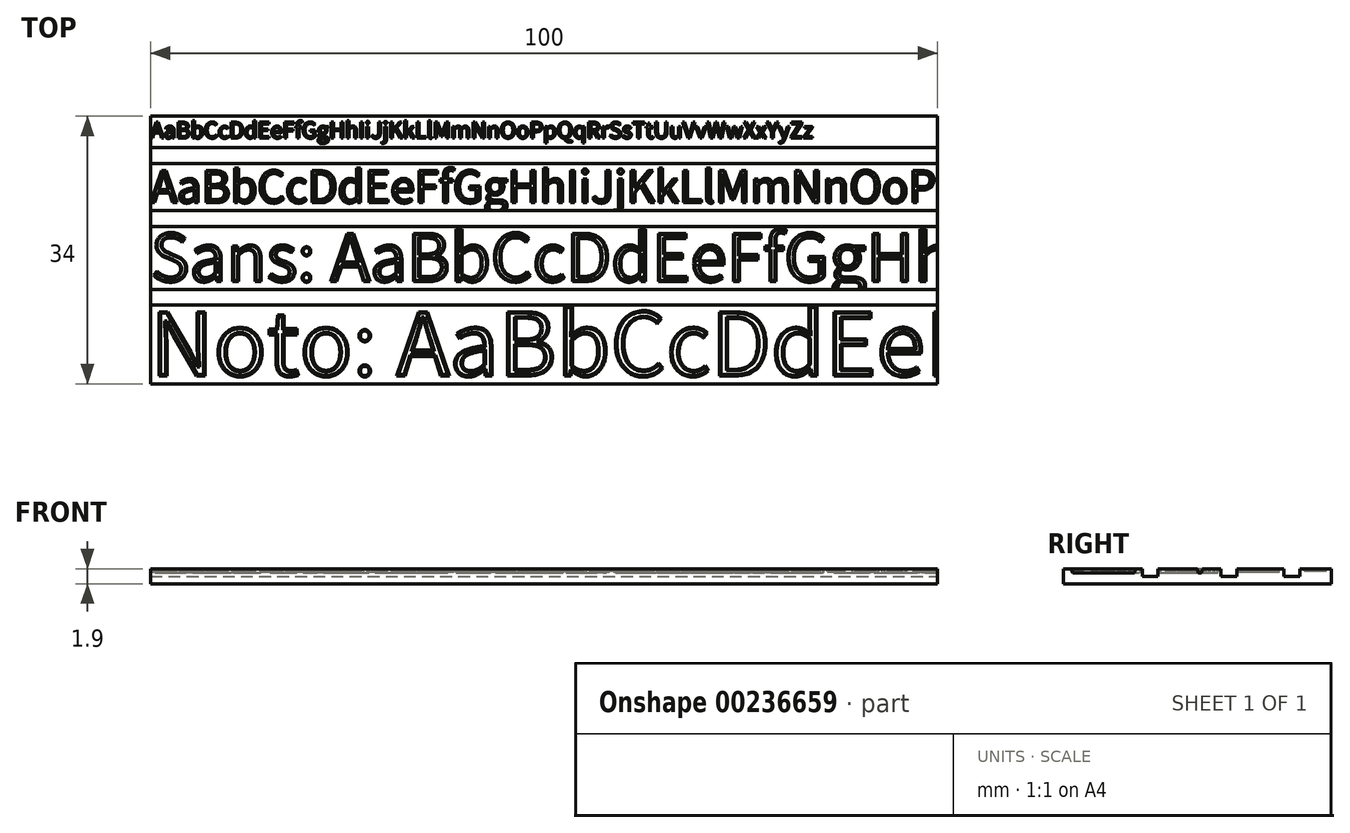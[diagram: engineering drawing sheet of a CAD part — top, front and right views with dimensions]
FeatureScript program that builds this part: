
annotation { "Feature Type Name" : "Feature", "Feature Type Description" : "" }
export const myFeature = defineFeature(function(context is Context, id is Id, definition is map)
    precondition{}
    {
        {
            var Q0;
            Q0=qCreatedBy(makeId("Top.planeOp"),FACE);
            var sketch = newSketch(context, id + "F0", { "sketchPlane" : qUnion([Q0])});
            skLineSegment(sketch, "E0.bottom", {"start": v(0, 0) * mm, "end": v(100, 0) * mm});
            skLineSegment(sketch, "E0.top", {"start": v(0, 34) * mm, "end": v(100, 34) * mm});
            skLineSegment(sketch, "E0.left", {"start": v(0, 0) * mm, "end": v(0, 34) * mm});
            skLineSegment(sketch, "E0.right", {"start": v(100, 0) * mm, "end": v(100, 34) * mm});
            skSolve(sketch);
        }
        {
            var Q0;
            Q0=makeQuery(id+"F0.imprint","IMPRINT",FACE,{"disambiguationData":[TD([[makeQuery(id+"F0.imprint","IMPRINT",EDGE,{"derivedFrom":sQuery(id+"F0.wireOp",EDGE,"E0.bottom")}),1.0]])]});
            extrude(context, id + "F1", {"entities" : qUnion([Q0]), "depth" : 0.9 * mm});
        }
        {
            var Q0;
            Q0=makeQuery(id+"F1.opExtrude","CAP_FACE",FACE,{"disambiguationData":[OSD([sQuery(id+"F0.wireOp",EDGE,"E0.bottom"),sQuery(id+"F0.wireOp",EDGE,"E0.top"),sQuery(id+"F0.wireOp",EDGE,"E0.left"),sQuery(id+"F0.wireOp",EDGE,"E0.right")])],"isStart":false});
            var sketch = newSketch(context, id + "F2", { "sketchPlane" : qUnion([Q0])});
            skLineSegment(sketch, "E1.bottom", {"start": v(0, 0) * mm, "end": v(100, 0) * mm});
            skLineSegment(sketch, "E1.top", {"start": v(0, 10) * mm, "end": v(100, 10) * mm});
            skLineSegment(sketch, "E1.left", {"start": v(0, 0) * mm, "end": v(0, 10) * mm});
            skLineSegment(sketch, "E1.right", {"start": v(100, 0) * mm, "end": v(100, 10) * mm});
            skLineSegment(sketch, "E2.bottom", {"start": v(0, 12) * mm, "end": v(100, 12) * mm});
            skLineSegment(sketch, "E2.top", {"start": v(0, 20) * mm, "end": v(100, 20) * mm});
            skLineSegment(sketch, "E2.left", {"start": v(0, 12) * mm, "end": v(0, 20) * mm});
            skLineSegment(sketch, "E2.right", {"start": v(100, 12) * mm, "end": v(100, 20) * mm});
            skLineSegment(sketch, "E3.bottom", {"start": v(0, 22) * mm, "end": v(100, 22) * mm});
            skLineSegment(sketch, "E3.top", {"start": v(0, 28) * mm, "end": v(100, 28) * mm});
            skLineSegment(sketch, "E3.left", {"start": v(0, 22) * mm, "end": v(0, 28) * mm});
            skLineSegment(sketch, "E3.right", {"start": v(100, 22) * mm, "end": v(100, 28) * mm});
            skLineSegment(sketch, "E4.bottom", {"start": v(0, 30) * mm, "end": v(100, 30) * mm});
            skLineSegment(sketch, "E4.top", {"start": v(0, 34) * mm, "end": v(100, 34) * mm});
            skLineSegment(sketch, "E4.left", {"start": v(0, 30) * mm, "end": v(0, 34) * mm});
            skLineSegment(sketch, "E4.right", {"start": v(100, 30) * mm, "end": v(100, 34) * mm});
            skSolve(sketch);
        }
        {
            var Q0;
            Q0 = qSketchRegion(id + "F2", true);
            extrude(context, id + "F3", {"entities" : qUnion([Q0]), "operationType" : NewBodyOperationType.ADD, "depth" : 1 * mm});
        }
        {
            var Q0;
            Q0=makeQuery(id+"F3.opExtrude","CAP_FACE",FACE,{"disambiguationData":[OSD([sQuery(id+"F2.wireOp",EDGE,"E1.bottom"),sQuery(id+"F2.wireOp",EDGE,"E1.top"),sQuery(id+"F2.wireOp",EDGE,"E1.left"),sQuery(id+"F2.wireOp",EDGE,"E1.right")])],"isStart":false});
            var sketch = newSketch(context, id + "F4", { "sketchPlane" : qUnion([Q0])});
            skText(sketch, "E5", { "text": "Noto: AaBbCcDdEeFfGgHhIiJjKkLlMmNnOoPpQqRrSsTtUuVvWwXxYyZz", "fontName": "NotoSansCJKjp-Regular.otf"});
            const initialGuessF4  = {"E5": [0, 0.001, 1, 0, 0.008]};
            skSetInitialGuess(sketch, initialGuessF4);
            skSolve(sketch);
        }
        {
            var Q0;
            Q0 = qSketchRegion(id + "F4", true);
            extrude(context, id + "F5", {"entities" : qUnion([Q0]), "operationType" : NewBodyOperationType.REMOVE, "oppositeDirection" : true, "depth" : 0.5 * mm, "hasDraft" : true, "draftAngle" : 20 * degree, "draftPullDirection" : true});
        }
        {
            var Q0;
            Q0=makeQuery(id+"F3.opExtrude","CAP_FACE",FACE,{"disambiguationData":[OSD([sQuery(id+"F2.wireOp",EDGE,"E2.bottom"),sQuery(id+"F2.wireOp",EDGE,"E2.top"),sQuery(id+"F2.wireOp",EDGE,"E2.left"),sQuery(id+"F2.wireOp",EDGE,"E2.right")])],"isStart":false});
            var sketch = newSketch(context, id + "F6", { "sketchPlane" : qUnion([Q0])});
            skText(sketch, "E6", { "text": "Sans: AaBbCcDdEeFfGgHhIiJjKkLlMmNnOoPpQqRrSsTtUuVvWwXxYyZz", "fontName": "NotoSansCJKjp-Regular.otf"});
            const initialGuessF6  = {"E6": [0, 0.013, 1, 0, 0.006]};
            skSetInitialGuess(sketch, initialGuessF6);
            skSolve(sketch);
        }
        {
            var Q0;
            Q0 = qSketchRegion(id + "F6", true);
            extrude(context, id + "F7", {"entities" : qUnion([Q0]), "operationType" : NewBodyOperationType.REMOVE, "oppositeDirection" : true, "depth" : 0.5 * mm, "hasDraft" : true, "draftAngle" : 15 * degree, "draftPullDirection" : true});
        }
        {
            var Q0;
            Q0=makeQuery(id+"F3.opExtrude","CAP_FACE",FACE,{"disambiguationData":[OSD([sQuery(id+"F2.wireOp",EDGE,"E3.bottom"),sQuery(id+"F2.wireOp",EDGE,"E3.top"),sQuery(id+"F2.wireOp",EDGE,"E3.left"),sQuery(id+"F2.wireOp",EDGE,"E3.right")])],"isStart":false});
            var sketch = newSketch(context, id + "F8", { "sketchPlane" : qUnion([Q0])});
            skText(sketch, "E7", { "text": "AaBbCcDdEeFfGgHhIiJjKkLlMmNnOoPpQqRrSsTtUuVvWwXxYyZz", "fontName": "NotoSansCJKjp-Regular.otf"});
            const initialGuessF8  = {"E7": [0, 0.023, 1, 0, 0.004]};
            skSetInitialGuess(sketch, initialGuessF8);
            skSolve(sketch);
        }
        {
            var Q0;
            Q0 = qSketchRegion(id + "F8", true);
            extrude(context, id + "F9", {"entities" : qUnion([Q0]), "operationType" : NewBodyOperationType.REMOVE, "oppositeDirection" : true, "depth" : 0.4 * mm, "hasDraft" : true, "draftAngle" : 10 * degree, "draftPullDirection" : true});
        }
        {
            var Q0;
            Q0=makeQuery(id+"F3.opExtrude","CAP_FACE",FACE,{"disambiguationData":[OSD([sQuery(id+"F2.wireOp",EDGE,"E4.bottom"),sQuery(id+"F2.wireOp",EDGE,"E4.top"),sQuery(id+"F2.wireOp",EDGE,"E4.left"),sQuery(id+"F2.wireOp",EDGE,"E4.right")])],"isStart":false});
            var sketch = newSketch(context, id + "F10", { "sketchPlane" : qUnion([Q0])});
            skText(sketch, "E8", { "text": "AaBbCcDdEeFfGgHhIiJjKkLlMmNnOoPpQqRrSsTtUuVvWwXxYyZz", "fontName": "NotoSansCJKjp-Regular.otf"});
            const initialGuessF10  = {"E8": [0, 0.0312, 1, 0, 0.002]};
            skSetInitialGuess(sketch, initialGuessF10);
            skSolve(sketch);
        }
        {
            var Q0;
            Q0 = qSketchRegion(id + "F10", true);
            extrude(context, id + "F11", {"entities" : qUnion([Q0]), "operationType" : NewBodyOperationType.REMOVE, "oppositeDirection" : true, "depth" : 0.3 * mm, "hasDraft" : true, "draftAngle" : 10 * degree, "draftPullDirection" : true});
        }
    });
